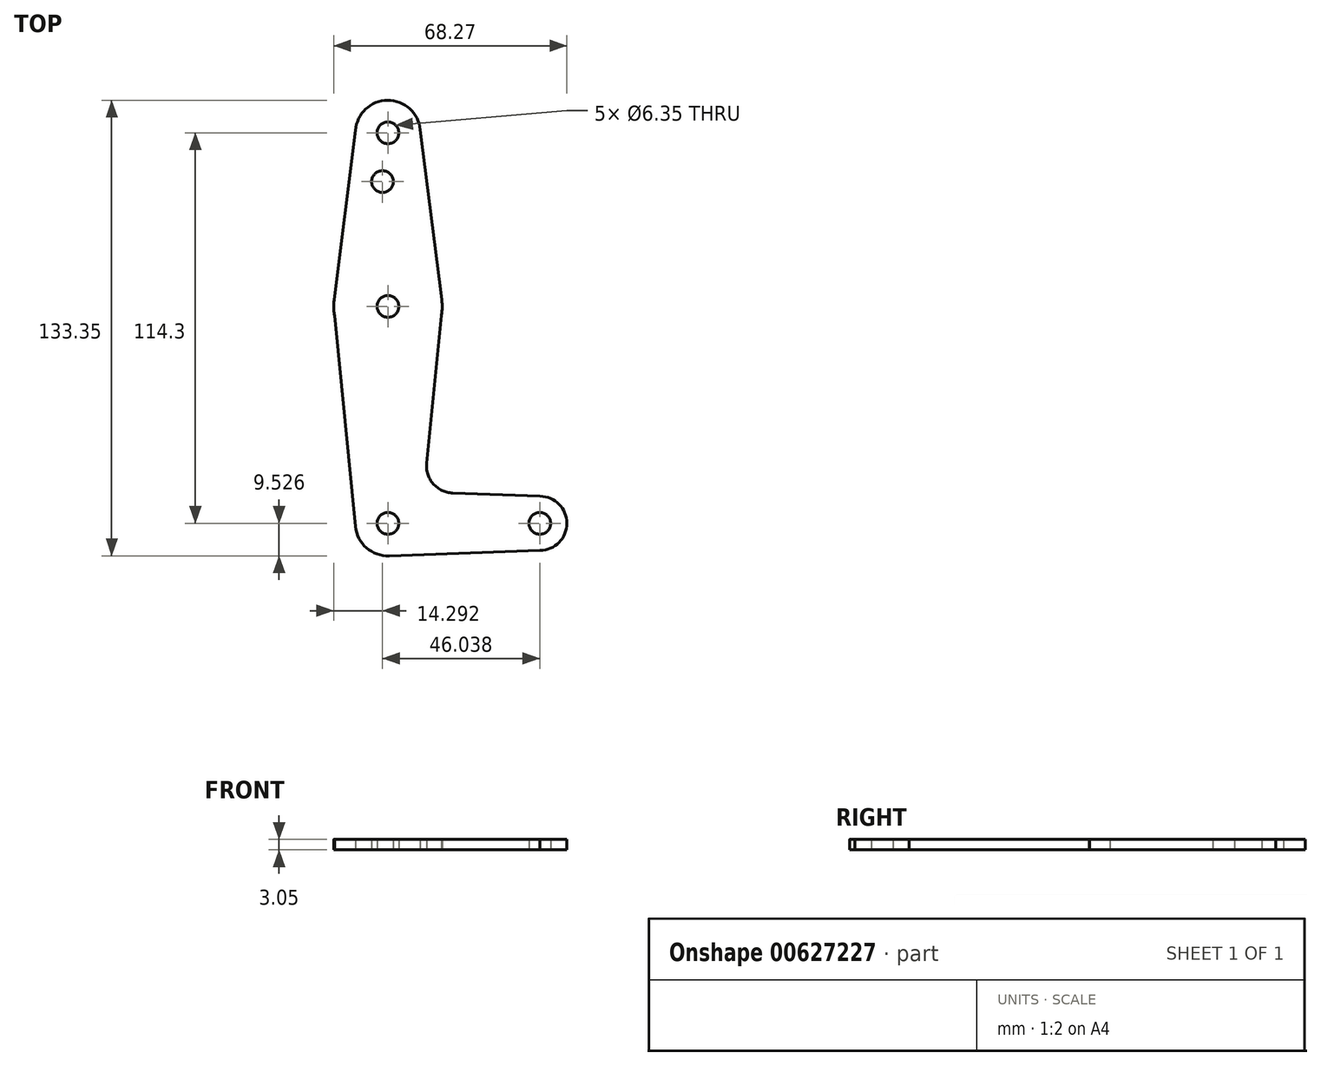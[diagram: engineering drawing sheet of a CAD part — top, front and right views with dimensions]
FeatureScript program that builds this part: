
annotation { "Feature Type Name" : "Feature", "Feature Type Description" : "" }
export const myFeature = defineFeature(function(context is Context, id is Id, definition is map)
    precondition{}
    {
        {
            var Q0;
            Q0=qCreatedBy(makeId("Top.planeOp"),FACE);
            var sketch = newSketch(context, id + "F0", { "sketchPlane" : qUnion([Q0])});
            skLineSegment(sketch, "E0", {"start": v(-44.95, 59.57) * mm, "end": v(-44.95, 8.77) * mm, "construction": true});
            skLineSegment(sketch, "E1", {"start": v(-44.95, 8.77) * mm, "end": v(-44.95, -54.73) * mm, "construction": true});
            skLineSegment(sketch, "E2", {"start": v(-44.95, -54.73) * mm, "end": v(-0.5, -54.73) * mm, "construction": true});
            skCircle(sketch, "E3", {"center": v(-44.95, 59.57) * mm, "radius": 9.53 * mm});
            skCircle(sketch, "E4", {"center": v(-44.95, 8.77) * mm, "radius": 15.88 * mm});
            skCircle(sketch, "E5", {"center": v(-44.95, -54.73) * mm, "radius": 9.53 * mm});
            skCircle(sketch, "E6", {"center": v(-0.5, -54.73) * mm, "radius": 7.94 * mm});
            skLineSegment(sketch, "E7", {"start": v(0, -46.81) * mm, "end": v(-26, -45.88) * mm});
            skLineSegment(sketch, "E8", {"start": v(0, -62.66) * mm, "end": v(-44.61, -64.25) * mm});
            skLineSegment(sketch, "E9", {"start": v(-54.45, 60.25) * mm, "end": v(-60.7, 10.75) * mm});
            skLineSegment(sketch, "E10", {"start": v(-35.54, 61.04) * mm, "end": v(-29.2, 10.75) * mm});
            skLineSegment(sketch, "E11", {"start": v(-60.6, 6.11) * mm, "end": v(-54.43, -55.68) * mm});
            skLineSegment(sketch, "E12", {"start": v(-29.3, 6.07) * mm, "end": v(-33.62, -37.15) * mm});
            skCircle(sketch, "E13", {"center": v(-44.95, 59.57) * mm, "radius": 3.18 * mm});
            skCircle(sketch, "E14", {"center": v(-46.54, 45.3) * mm, "radius": 3.18 * mm});
            skCircle(sketch, "E15", {"center": v(-44.95, 8.77) * mm, "radius": 3.17 * mm});
            skCircle(sketch, "E16", {"center": v(-44.95, -54.73) * mm, "radius": 3.18 * mm});
            skCircle(sketch, "E17", {"center": v(-0.5, -54.73) * mm, "radius": 3.18 * mm});
            skArc(sketch, "E18.filletArc", {"start": v(-33.62, -37.15) * mm, "mid": v(-31.7, -43.17) * mm, "end": v(-26, -45.88) * mm});
            skSolve(sketch);
        }
        {
            var Q0;
            Q0 = qSketchRegion(id + "F0", true);
            extrude(context, id + "F1", {"entities" : qUnion([Q0]), "depth" : 3.05 * mm, "offsetDistance" : 25.4 * mm});
        }
    });
